# Revit family: HOSPITAIR PACK - 11 bar - 15 bar
name_source: partatom
category: Equipement de génie climatique
revit_build: Autodesk Revit 2018 (Build: 20170223_1515(x64)
units: mm (PartAtom-declared; Revit-internal decimal feet)

## family parameters
Basée sur le plan de construction = Non
Classification = Aucun
Cote de connecteur circulaire = Utiliser le diamètre
Couper avec des vides une fois chargée = Non
Partagée = Non
Point de calcul de pièce = Non
Toujours verticalement = Oui
Type d'élément = Normal

## types (30) — shared parameters
COS_PHI_COFFRET = 0.9
COS_PHI_COMPRESSEUR = 0.9
NBR_POLES_COFFRET_CONNEXION_X' = 1
NBR_POLES_COFFRET_CONNEXION_Y' = 1
NBR_POLES_COFFRET_X = 1
NBR_POLES_COFFRET_Y = 1
NBR_POLES_COMPRESSEUR = 3
PUISS_ELECT_COFFRET = 0 kW
PUISS_ELECT_COFFRET' = 0 kW
TENSION_ALIM_COMPRESSEUR = 400 V

## per-type parameters (varying)
- HOSPITAIR PACK - 11 bar - MVX4 - Principal: BRANCHEMENT_TERRE_COFFRET_CONNEXION_X'=Non; BRANCHEMENT_TERRE_COFFRET_CONNEXION_Y'=Non; BRANCHEMENT_TERRE_COFFRET_X=Oui; BRANCHEMENT_TERRE_COFFRET_Y=Oui; BRANCHEMENT_TERRE_COMPRESSEUR=Oui; COFFRET ELEC STANDARD PM2=Oui; COMPRESSEUR=HOSPITAIR G - MVX 4-5 - MVA 9 - MVB 12-16 - MVC 19-23 : MVX 4; CONNEXION X'_Y'=Non; Chaine de traitement ...AD5035=Oui; Chaine de traitement ...AD5065=Non; Chaine de traitement ...AD5130=Non; Chaine de traitement ...AD5195=Non; DESCR_ALIM_COFFRET_CONNEXION_X'=NE PAS UTILISER; DESCR_ALIM_COFFRET_CONNEXION_Y'=NE PAS UTILISER; DESCR_ALIM_COFFRET_X=Alimentation électrique, 3G0.75mm²; DESCR_ALIM_COFFRET_Y=Alimentation électrique, 3G0.75mm²; DESCR_ALIM_COMPRESSEUR=Alimentation électrique, 4G2.5mm²; DESCR_REFOUL=Refoulement Air; 29m3/h; G1/2"FEM; DIAM_REFOUL_AIR=15 mm  [stored 0.0492126 ft]; Debit_refoulement_air=29.0 m³/h; HAUTEUR=1340 mm; HAUTEUR_COFFRET=1080 mm  [stored 3.54331 ft]; HAUTEUR_SORTIE_AIR=1372 mm; LARGEUR=600 mm  [stored 1.9685 ft]; LARGEUR_COFFRET_GAUCHE=300 mm  [stored 0.984252 ft]; LARGEUR_SORTIE_AIR=25 mm  [stored 0.082021 ft]; LONGUEUR=860 mm; LONGUEUR_COFFRET_GAUCHE=344 mm; MAINTENANCE_ZONE_ARRIERE=1135 mm; MAINTENANCE_ZONE_AVANT=720 mm; MAINTENANCE_ZONE_GAUCHE-DROITE=2190 mm; MAINTENANCE_ZONE_HAUTEUR=1780 mm; NEUTRE_COFFRET_CONNEXION_X'=Non; NEUTRE_COFFRET_CONNEXION_Y'=Non; NEUTRE_COFFRET_X=Oui; NEUTRE_COFFRET_Y=Oui; NIVEAU_SONORE(dB(A))=62; POIDS(Kg)=170 mm  [stored 0.557743 ft]; PUISS_APPARENTE_COFFRET=333 VA; PUISS_APPARENTE_COFFRET'=0 VA; PUISS_APPARENTE_COMPRESSEUR=4444 VA; PUISS_ELECT_COMPRESSEUR=4 kW; TENSION_ALIM_COFFRET=230 V; Zone de maintenance=Oui
- HOSPITAIR PACK - 11 bar - MVX5 - Principal: BRANCHEMENT_TERRE_COFFRET_CONNEXION_X'=Non; BRANCHEMENT_TERRE_COFFRET_CONNEXION_Y'=Non; BRANCHEMENT_TERRE_COFFRET_X=Oui; BRANCHEMENT_TERRE_COFFRET_Y=Oui; BRANCHEMENT_TERRE_COMPRESSEUR=Oui; COFFRET ELEC STANDARD PM2=Oui; COMPRESSEUR=HOSPITAIR G - MVX 4-5 - MVA 9 - MVB 12-16 - MVC 19-23 : MVX 5; CONNEXION X'_Y'=Non; Chaine de traitement ...AD5035=Non; Chaine de traitement ...AD5065=Oui; Chaine de traitement ...AD5130=Non; Chaine de traitement ...AD5195=Non; DESCR_ALIM_COFFRET_CONNEXION_X'=NE PAS UTILISER; DESCR_ALIM_COFFRET_CONNEXION_Y'=NE PAS UTILISER; DESCR_ALIM_COFFRET_X=Alimentation électrique, 3G0.75mm²; DESCR_ALIM_COFFRET_Y=Alimentation électrique, 3G0.75mm²; DESCR_ALIM_COMPRESSEUR=Alimentation électrique, 4G2.5mm²; DESCR_REFOUL=Refoulement Air; 40m3/h; G1/2"FEM; DIAM_REFOUL_AIR=15 mm  [stored 0.0492126 ft]; Debit_refoulement_air=40.0 m³/h; HAUTEUR=1430 mm; HAUTEUR_COFFRET=1365 mm; HAUTEUR_SORTIE_AIR=1662 mm; LARGEUR=600 mm  [stored 1.9685 ft]; LARGEUR_COFFRET_GAUCHE=300 mm  [stored 0.984252 ft]; LARGEUR_SORTIE_AIR=20 mm  [stored 0.0656168 ft]; LONGUEUR=870 mm  [stored 2.85433 ft]; LONGUEUR_COFFRET_GAUCHE=344 mm; MAINTENANCE_ZONE_ARRIERE=1135 mm; MAINTENANCE_ZONE_AVANT=720 mm; MAINTENANCE_ZONE_GAUCHE-DROITE=2190 mm; MAINTENANCE_ZONE_HAUTEUR=2065 mm; NEUTRE_COFFRET_CONNEXION_X'=Non; NEUTRE_COFFRET_CONNEXION_Y'=Non; NEUTRE_COFFRET_X=Oui; NEUTRE_COFFRET_Y=Oui; NIVEAU_SONORE(dB(A))=64; POIDS(Kg)=185 mm  [stored 0.606955 ft]; PUISS_APPARENTE_COFFRET=333 VA; PUISS_APPARENTE_COFFRET'=0 VA; PUISS_APPARENTE_COMPRESSEUR=6111 VA; PUISS_ELECT_COMPRESSEUR=6 kW; TENSION_ALIM_COFFRET=230 V; Zone de maintenance=Oui
- HOSPITAIR PACK - 11 bar - MVA9 - Principal: BRANCHEMENT_TERRE_COFFRET_CONNEXION_X'=Non; BRANCHEMENT_TERRE_COFFRET_CONNEXION_Y'=Non; BRANCHEMENT_TERRE_COFFRET_X=Oui; BRANCHEMENT_TERRE_COFFRET_Y=Oui; BRANCHEMENT_TERRE_COMPRESSEUR=Oui; COFFRET ELEC STANDARD PM2=Oui; COMPRESSEUR=HOSPITAIR G - MVX 4-5 - MVA 9 - MVB 12-16 - MVC 19-23 : MVA 9; CONNEXION X'_Y'=Non; Chaine de traitement ...AD5035=Non; Chaine de traitement ...AD5065=Oui; Chaine de traitement ...AD5130=Non; Chaine de traitement ...AD5195=Non; DESCR_ALIM_COFFRET_CONNEXION_X'=NE PAS UTILISER; DESCR_ALIM_COFFRET_CONNEXION_Y'=NE PAS UTILISER; DESCR_ALIM_COFFRET_X=Alimentation électrique, 3G0.75mm²; DESCR_ALIM_COFFRET_Y=Alimentation électrique, 3G0.75mm²; DESCR_ALIM_COMPRESSEUR=Alimentation électrique, 4G4mm²; DESCR_REFOUL=Refoulement Air; 65m3/h; G1/2"FEM; DIAM_REFOUL_AIR=15 mm  [stored 0.0492126 ft]; Debit_refoulement_air=65.0 m³/h; HAUTEUR=1630 mm; HAUTEUR_COFFRET=1365 mm; HAUTEUR_SORTIE_AIR=1662 mm; LARGEUR=640 mm  [stored 2.09974 ft]; LARGEUR_COFFRET_GAUCHE=300 mm  [stored 0.984252 ft]; LARGEUR_SORTIE_AIR=20 mm  [stored 0.0656168 ft]; LONGUEUR=1000 mm  [stored 3.28084 ft]; LONGUEUR_COFFRET_GAUCHE=344 mm; MAINTENANCE_ZONE_ARRIERE=1293 mm; MAINTENANCE_ZONE_AVANT=720 mm; MAINTENANCE_ZONE_GAUCHE-DROITE=2230 mm; MAINTENANCE_ZONE_HAUTEUR=2065 mm; NEUTRE_COFFRET_CONNEXION_X'=Non; NEUTRE_COFFRET_CONNEXION_Y'=Non; NEUTRE_COFFRET_X=Oui; NEUTRE_COFFRET_Y=Oui; NIVEAU_SONORE(dB(A))=65; POIDS(Kg)=290 mm  [stored 0.951444 ft]; PUISS_APPARENTE_COFFRET=333 VA; PUISS_APPARENTE_COFFRET'=0 VA; PUISS_APPARENTE_COMPRESSEUR=8333 VA; PUISS_ELECT_COMPRESSEUR=8 kW; TENSION_ALIM_COFFRET=230 V; Zone de maintenance=Oui
- HOSPITAIR PACK - 11 bar - MVX3 -  Principal: BRANCHEMENT_TERRE_COFFRET_CONNEXION_X'=Non; BRANCHEMENT_TERRE_COFFRET_CONNEXION_Y'=Non; BRANCHEMENT_TERRE_COFFRET_X=Oui; BRANCHEMENT_TERRE_COFFRET_Y=Oui; BRANCHEMENT_TERRE_COMPRESSEUR=Oui; COFFRET ELEC STANDARD PM2=Oui; COMPRESSEUR=HOSPITAIR G - MVX 4-5 - MVA 9 - MVB 12-16 - MVC 19-23 : MVX 4; CONNEXION X'_Y'=Non; Chaine de traitement ...AD5035=Oui; Chaine de traitement ...AD5065=Non; Chaine de traitement ...AD5130=Non; Chaine de traitement ...AD5195=Non; DESCR_ALIM_COFFRET_CONNEXION_X'=NE PAS UTILISER; DESCR_ALIM_COFFRET_CONNEXION_Y'=NE PAS UTILISER; DESCR_ALIM_COFFRET_X=Alimentation électrique, 3G0.75mm²; DESCR_ALIM_COFFRET_Y=Alimentation électrique, 3G0.75mm²; DESCR_ALIM_COMPRESSEUR=Alimentation électrique, 4G2.5mm²; DESCR_REFOUL=Refoulement Air; 22m3/h; G1/2"FEM; DIAM_REFOUL_AIR=15 mm  [stored 0.0492126 ft]; Debit_refoulement_air=22.0 m³/h; HAUTEUR=1340 mm; HAUTEUR_COFFRET=1080 mm  [stored 3.54331 ft]; HAUTEUR_SORTIE_AIR=1372 mm; LARGEUR=600 mm  [stored 1.9685 ft]; LARGEUR_COFFRET_GAUCHE=300 mm  [stored 0.984252 ft]; LARGEUR_SORTIE_AIR=25 mm  [stored 0.082021 ft]; LONGUEUR=860 mm; LONGUEUR_COFFRET_GAUCHE=344 mm; MAINTENANCE_ZONE_ARRIERE=1135 mm; MAINTENANCE_ZONE_AVANT=720 mm; MAINTENANCE_ZONE_GAUCHE-DROITE=2190 mm; MAINTENANCE_ZONE_HAUTEUR=1780 mm; NEUTRE_COFFRET_CONNEXION_X'=Non; NEUTRE_COFFRET_CONNEXION_Y'=Non; NEUTRE_COFFRET_X=Oui; NEUTRE_COFFRET_Y=Oui; NIVEAU_SONORE(dB(A))=61; POIDS(Kg)=165 mm; PUISS_APPARENTE_COFFRET=333 VA; PUISS_APPARENTE_COFFRET'=0 VA; PUISS_APPARENTE_COMPRESSEUR=3333 VA; PUISS_ELECT_COMPRESSEUR=3 kW; TENSION_ALIM_COFFRET=230 V; Zone de maintenance=Oui
- HOSPITAIR PACK - 11 bar - MVX2 - Principal: BRANCHEMENT_TERRE_COFFRET_CONNEXION_X'=Non; BRANCHEMENT_TERRE_COFFRET_CONNEXION_Y'=Non; BRANCHEMENT_TERRE_COFFRET_X=Oui; BRANCHEMENT_TERRE_COFFRET_Y=Oui; BRANCHEMENT_TERRE_COMPRESSEUR=Oui; COFFRET ELEC STANDARD PM2=Oui; COMPRESSEUR=HOSPITAIR G - MVX 4-5 - MVA 9 - MVB 12-16 - MVC 19-23 : MVX 4; CONNEXION X'_Y'=Non; Chaine de traitement ...AD5035=Oui; Chaine de traitement ...AD5065=Non; Chaine de traitement ...AD5130=Non; Chaine de traitement ...AD5195=Non; DESCR_ALIM_COFFRET_CONNEXION_X'=NE PAS UTILISER; DESCR_ALIM_COFFRET_CONNEXION_Y'=NE PAS UTILISER; DESCR_ALIM_COFFRET_X=Alimentation électrique, 3G0.75mm²; DESCR_ALIM_COFFRET_Y=Alimentation électrique, 3G0.75mm²; DESCR_ALIM_COMPRESSEUR=Alimentation électrique, 4G2.5mm²; DESCR_REFOUL=Refoulement Air; 16m3/h; G1/2"FEM; DIAM_REFOUL_AIR=15 mm  [stored 0.0492126 ft]; Debit_refoulement_air=16.0 m³/h; HAUTEUR=1340 mm; HAUTEUR_COFFRET=1080 mm  [stored 3.54331 ft]; HAUTEUR_SORTIE_AIR=1372 mm; LARGEUR=600 mm  [stored 1.9685 ft]; LARGEUR_COFFRET_GAUCHE=300 mm  [stored 0.984252 ft]; LARGEUR_SORTIE_AIR=25 mm  [stored 0.082021 ft]; LONGUEUR=860 mm; LONGUEUR_COFFRET_GAUCHE=344 mm; MAINTENANCE_ZONE_ARRIERE=1135 mm; MAINTENANCE_ZONE_AVANT=720 mm; MAINTENANCE_ZONE_GAUCHE-DROITE=2190 mm; MAINTENANCE_ZONE_HAUTEUR=1780 mm; NEUTRE_COFFRET_CONNEXION_X'=Non; NEUTRE_COFFRET_CONNEXION_Y'=Non; NEUTRE_COFFRET_X=Oui; NEUTRE_COFFRET_Y=Oui; NIVEAU_SONORE(dB(A))=60; POIDS(Kg)=165 mm; PUISS_APPARENTE_COFFRET=333 VA; PUISS_APPARENTE_COFFRET'=0 VA; PUISS_APPARENTE_COMPRESSEUR=2444 VA; PUISS_ELECT_COMPRESSEUR=2 kW; TENSION_ALIM_COFFRET=230 V; Zone de maintenance=Non
- HOSPITAIR PACK - 11 bar - MVB12 - Principal: BRANCHEMENT_TERRE_COFFRET_CONNEXION_X'=Non; BRANCHEMENT_TERRE_COFFRET_CONNEXION_Y'=Non; BRANCHEMENT_TERRE_COFFRET_X=Oui; BRANCHEMENT_TERRE_COFFRET_Y=Oui; BRANCHEMENT_TERRE_COMPRESSEUR=Oui; COFFRET ELEC STANDARD PM2=Oui; COMPRESSEUR=HOSPITAIR G - MVX 4-5 - MVA 9 - MVB 12-16 - MVC 19-23 : MVB 12; CONNEXION X'_Y'=Non; Chaine de traitement ...AD5035=Non; Chaine de traitement ...AD5065=Non; Chaine de traitement ...AD5130=Oui; Chaine de traitement ...AD5195=Non; DESCR_ALIM_COFFRET_CONNEXION_X'=NE PAS UTILISER; DESCR_ALIM_COFFRET_CONNEXION_Y'=NE PAS UTILISER; DESCR_ALIM_COFFRET_X=Alimentation électrique, 3G0.75mm²; DESCR_ALIM_COFFRET_Y=Alimentation électrique, 3G0.75mm²; DESCR_ALIM_COMPRESSEUR=Alimentation électrique, 4G6mm²; DESCR_REFOUL=Refoulement Air; 100m3/h; G3/4"FEM; DIAM_REFOUL_AIR=20 mm  [stored 0.0656168 ft]; Debit_refoulement_air=100.0 m³/h; HAUTEUR=1350 mm; HAUTEUR_COFFRET=1365 mm; HAUTEUR_SORTIE_AIR=1662 mm; LARGEUR=750 mm  [stored 2.46063 ft]; LARGEUR_COFFRET_GAUCHE=370 mm  [stored 1.21391 ft]; LARGEUR_SORTIE_AIR=95 mm  [stored 0.31168 ft]; LONGUEUR=1100 mm; LONGUEUR_COFFRET_GAUCHE=344 mm; MAINTENANCE_ZONE_ARRIERE=1398 mm; MAINTENANCE_ZONE_AVANT=792.5 mm; MAINTENANCE_ZONE_GAUCHE-DROITE=2350 mm; MAINTENANCE_ZONE_HAUTEUR=2065 mm; NEUTRE_COFFRET_CONNEXION_X'=Non; NEUTRE_COFFRET_CONNEXION_Y'=Non; NEUTRE_COFFRET_X=Oui; NEUTRE_COFFRET_Y=Oui; NIVEAU_SONORE(dB(A))=64; POIDS(Kg)=375 mm  [stored 1.23031 ft]; PUISS_APPARENTE_COFFRET=333 VA; PUISS_APPARENTE_COFFRET'=0 VA; PUISS_APPARENTE_COMPRESSEUR=12222 VA; PUISS_ELECT_COMPRESSEUR=11 kW; TENSION_ALIM_COFFRET=230 V; Zone de maintenance=Oui
- HOSPITAIR PACK - 11 bar - MVC19 - Principal: BRANCHEMENT_TERRE_COFFRET_CONNEXION_X'=Oui; BRANCHEMENT_TERRE_COFFRET_CONNEXION_Y'=Oui; BRANCHEMENT_TERRE_COFFRET_X=Non; BRANCHEMENT_TERRE_COFFRET_Y=Non; BRANCHEMENT_TERRE_COMPRESSEUR=Oui; COFFRET ELEC STANDARD PM2=Oui; COMPRESSEUR=HOSPITAIR G - MVX 4-5 - MVA 9 - MVB 12-16 - MVC 19-23 : MVC 19; CONNEXION X'_Y'=Oui; Chaine de traitement ...AD5035=Non; Chaine de traitement ...AD5065=Non; Chaine de traitement ...AD5130=Non; Chaine de traitement ...AD5195=Oui; DESCR_ALIM_COFFRET_CONNEXION_X'=Alimentation électrique, 3G0.75mm²; DESCR_ALIM_COFFRET_CONNEXION_Y'=Alimentation électrique, 3G0.75mm²; DESCR_ALIM_COFFRET_X=NE PAS UTILISER; DESCR_ALIM_COFFRET_Y=NE PAS UTILISER; DESCR_ALIM_COMPRESSEUR=Alimentation électrique, 4G10mm²; DESCR_REFOUL=Refoulement Air; 179m3/h; G3/4"FEM; DIAM_REFOUL_AIR=20 mm  [stored 0.0656168 ft]; Debit_refoulement_air=179.0 m³/h; HAUTEUR=1670 mm; HAUTEUR_COFFRET=1550 mm; HAUTEUR_SORTIE_AIR=1662 mm; LARGEUR=890 mm  [stored 2.91995 ft]; LARGEUR_COFFRET_GAUCHE=400 mm  [stored 1.31234 ft]; LARGEUR_SORTIE_AIR=10 mm  [stored 0.0328084 ft]; LONGUEUR=1870 mm; LONGUEUR_COFFRET_GAUCHE=1048 mm; MAINTENANCE_ZONE_ARRIERE=1593 mm; MAINTENANCE_ZONE_AVANT=792.5 mm; MAINTENANCE_ZONE_GAUCHE-DROITE=2400 mm; MAINTENANCE_ZONE_HAUTEUR=2250 mm; NEUTRE_COFFRET_CONNEXION_X'=Oui; NEUTRE_COFFRET_CONNEXION_Y'=Oui; NEUTRE_COFFRET_X=Non; NEUTRE_COFFRET_Y=Non; NIVEAU_SONORE(dB(A))=67; POIDS(Kg)=660 mm  [stored 2.16535 ft]; PUISS_APPARENTE_COFFRET=0 VA; PUISS_APPARENTE_COFFRET'=333 VA; PUISS_APPARENTE_COMPRESSEUR=20556 VA; PUISS_ELECT_COMPRESSEUR=19 kW; TENSION_ALIM_COFFRET=230 V; Zone de maintenance=Oui
- HOSPITAIR PACK - 11 bar - MVB16 - Principal: BRANCHEMENT_TERRE_COFFRET_CONNEXION_X'=Non; BRANCHEMENT_TERRE_COFFRET_CONNEXION_Y'=Non; BRANCHEMENT_TERRE_COFFRET_X=Oui; BRANCHEMENT_TERRE_COFFRET_Y=Oui; BRANCHEMENT_TERRE_COMPRESSEUR=Oui; COFFRET ELEC STANDARD PM2=Oui; COMPRESSEUR=HOSPITAIR G - MVX 4-5 - MVA 9 - MVB 12-16 - MVC 19-23 : MVB 16; CONNEXION X'_Y'=Non; Chaine de traitement ...AD5035=Non; Chaine de traitement ...AD5065=Non; Chaine de traitement ...AD5130=Oui; Chaine de traitement ...AD5195=Non; DESCR_ALIM_COFFRET_CONNEXION_X'=NE PAS UTILISER; DESCR_ALIM_COFFRET_CONNEXION_Y'=NE PAS UTILISER; DESCR_ALIM_COFFRET_X=Alimentation électrique, 3G0.75mm²; DESCR_ALIM_COFFRET_Y=Alimentation électrique, 3G0.75mm²; DESCR_ALIM_COMPRESSEUR=Alimentation électrique, 4G10mm²; DESCR_REFOUL=Refoulement Air; 126m3/h; G3/4"FEM; DIAM_REFOUL_AIR=20 mm  [stored 0.0656168 ft]; Debit_refoulement_air=126.0 m³/h; HAUTEUR=1350 mm; HAUTEUR_COFFRET=1365 mm; HAUTEUR_SORTIE_AIR=1662 mm; LARGEUR=750 mm  [stored 2.46063 ft]; LARGEUR_COFFRET_GAUCHE=370 mm  [stored 1.21391 ft]; LARGEUR_SORTIE_AIR=95 mm  [stored 0.31168 ft]; LONGUEUR=1250 mm  [stored 4.10105 ft]; LONGUEUR_COFFRET_GAUCHE=344 mm; MAINTENANCE_ZONE_ARRIERE=1398 mm; MAINTENANCE_ZONE_AVANT=792.5 mm; MAINTENANCE_ZONE_GAUCHE-DROITE=2350 mm; MAINTENANCE_ZONE_HAUTEUR=2065 mm; NEUTRE_COFFRET_CONNEXION_X'=Non; NEUTRE_COFFRET_CONNEXION_Y'=Non; NEUTRE_COFFRET_X=Oui; NEUTRE_COFFRET_Y=Oui; NIVEAU_SONORE(dB(A))=65; POIDS(Kg)=480 mm  [stored 1.5748 ft]; PUISS_APPARENTE_COFFRET=333 VA; PUISS_APPARENTE_COFFRET'=0 VA; PUISS_APPARENTE_COMPRESSEUR=16667 VA; PUISS_ELECT_COMPRESSEUR=15 kW; TENSION_ALIM_COFFRET=230 V; Zone de maintenance=Oui
- HOSPITAIR PACK - 15 bar - MVC23 - Principal: BRANCHEMENT_TERRE_COFFRET_CONNEXION_X'=Oui; BRANCHEMENT_TERRE_COFFRET_CONNEXION_Y'=Oui; BRANCHEMENT_TERRE_COFFRET_X=Non; BRANCHEMENT_TERRE_COFFRET_Y=Non; BRANCHEMENT_TERRE_COMPRESSEUR=Oui; COFFRET ELEC STANDARD PM2=Oui; COMPRESSEUR=HOSPITAIR G - MVX 4-5 - MVA 9 - MVB 12-16 - MVC 19-23 : MVC 23; CONNEXION X'_Y'=Oui; Chaine de traitement ...AD5035=Non; Chaine de traitement ...AD5065=Non; Chaine de traitement ...AD5130=Non; Chaine de traitement ...AD5195=Oui; DESCR_ALIM_COFFRET_CONNEXION_X'=Alimentation électrique, 3G0.75mm²; DESCR_ALIM_COFFRET_CONNEXION_Y'=Alimentation électrique, 3G0.75mm²; DESCR_ALIM_COFFRET_X=NE PAS UTILISER; DESCR_ALIM_COFFRET_Y=NE PAS UTILISER; DESCR_ALIM_COMPRESSEUR=Alimentation électrique, 4G16mm²; DESCR_REFOUL=Refoulement Air; 174m3/h; G3/4"FEM; DIAM_REFOUL_AIR=20 mm  [stored 0.0656168 ft]; Debit_refoulement_air=174.0 m³/h; HAUTEUR=1670 mm; HAUTEUR_COFFRET=1550 mm; HAUTEUR_SORTIE_AIR=1662 mm; LARGEUR=890 mm  [stored 2.91995 ft]; LARGEUR_COFFRET_GAUCHE=400 mm  [stored 1.31234 ft]; LARGEUR_SORTIE_AIR=10 mm  [stored 0.0328084 ft]; LONGUEUR=1870 mm; LONGUEUR_COFFRET_GAUCHE=1048 mm; MAINTENANCE_ZONE_ARRIERE=1593 mm; MAINTENANCE_ZONE_AVANT=792.5 mm; MAINTENANCE_ZONE_GAUCHE-DROITE=2400 mm; MAINTENANCE_ZONE_HAUTEUR=2250 mm; NEUTRE_COFFRET_CONNEXION_X'=Oui; NEUTRE_COFFRET_CONNEXION_Y'=Oui; NEUTRE_COFFRET_X=Non; NEUTRE_COFFRET_Y=Non; NIVEAU_SONORE(dB(A))=69; POIDS(Kg)=690 mm  [stored 2.26378 ft]; PUISS_APPARENTE_COFFRET=0 VA; PUISS_APPARENTE_COFFRET'=333 VA; PUISS_APPARENTE_COMPRESSEUR=24444 VA; PUISS_ELECT_COMPRESSEUR=22 kW; TENSION_ALIM_COFFRET=230 V; Zone de maintenance=Oui
- HOSPITAIR PACK - 11 bar - MVX2 - Secondaire: BRANCHEMENT_TERRE_COFFRET_CONNEXION_X'=Non; BRANCHEMENT_TERRE_COFFRET_CONNEXION_Y'=Non; BRANCHEMENT_TERRE_COFFRET_X=Non; BRANCHEMENT_TERRE_COFFRET_Y=Non; BRANCHEMENT_TERRE_COMPRESSEUR=Non; COFFRET ELEC STANDARD PM2=Non; COMPRESSEUR=HOSPITAIR G - MVX 4-5 - MVA 9 - MVB 12-16 - MVC 19-23 : MVX 4; CONNEXION X'_Y'=Non; Chaine de traitement ...AD5035=Oui; Chaine de traitement ...AD5065=Non; Chaine de traitement ...AD5130=Non; Chaine de traitement ...AD5195=Non; DESCR_ALIM_COFFRET_CONNEXION_X'=NE PAS UTILISER; DESCR_ALIM_COFFRET_CONNEXION_Y'=NE PAS UTILISER; DESCR_ALIM_COFFRET_X=NE PAS UTILISER; DESCR_ALIM_COFFRET_Y=NE PAS UTILISER; DESCR_ALIM_COMPRESSEUR=Alimentation électrique, 4G2.5mm²; DESCR_REFOUL=Refoulement Air; 16m3/h; G1/2"FEM; DIAM_REFOUL_AIR=15 mm  [stored 0.0492126 ft]; Debit_refoulement_air=16.0 m³/h; HAUTEUR=1340 mm; HAUTEUR_COFFRET=1080 mm  [stored 3.54331 ft]; HAUTEUR_SORTIE_AIR=1372 mm; LARGEUR=600 mm  [stored 1.9685 ft]; LARGEUR_COFFRET_GAUCHE=300 mm  [stored 0.984252 ft]; LARGEUR_SORTIE_AIR=25 mm  [stored 0.082021 ft]; LONGUEUR=860 mm; LONGUEUR_COFFRET_GAUCHE=344 mm; MAINTENANCE_ZONE_ARRIERE=1135 mm; MAINTENANCE_ZONE_AVANT=720 mm; MAINTENANCE_ZONE_GAUCHE-DROITE=2190 mm; MAINTENANCE_ZONE_HAUTEUR=1780 mm; NEUTRE_COFFRET_CONNEXION_X'=Non; NEUTRE_COFFRET_CONNEXION_Y'=Non; NEUTRE_COFFRET_X=Non; NEUTRE_COFFRET_Y=Non; NIVEAU_SONORE(dB(A))=60; POIDS(Kg)=155 mm  [stored 0.50853 ft]; PUISS_APPARENTE_COFFRET=0 VA; PUISS_APPARENTE_COFFRET'=0 VA; PUISS_APPARENTE_COMPRESSEUR=2444 VA; PUISS_ELECT_COMPRESSEUR=2 kW; TENSION_ALIM_COFFRET=0 V; Zone de maintenance=Oui
- HOSPITAIR PACK - 11 bar - MVX3 - Secondaire: BRANCHEMENT_TERRE_COFFRET_CONNEXION_X'=Non; BRANCHEMENT_TERRE_COFFRET_CONNEXION_Y'=Non; BRANCHEMENT_TERRE_COFFRET_X=Non; BRANCHEMENT_TERRE_COFFRET_Y=Non; BRANCHEMENT_TERRE_COMPRESSEUR=Oui; COFFRET ELEC STANDARD PM2=Non; COMPRESSEUR=HOSPITAIR G - MVX 4-5 - MVA 9 - MVB 12-16 - MVC 19-23 : MVX 4; CONNEXION X'_Y'=Non; Chaine de traitement ...AD5035=Oui; Chaine de traitement ...AD5065=Non; Chaine de traitement ...AD5130=Non; Chaine de traitement ...AD5195=Non; DESCR_ALIM_COFFRET_CONNEXION_X'=NE PAS UTILISER; DESCR_ALIM_COFFRET_CONNEXION_Y'=NE PAS UTILISER; DESCR_ALIM_COFFRET_X=NE PAS UTILISER; DESCR_ALIM_COFFRET_Y=NE PAS UTILISER; DESCR_ALIM_COMPRESSEUR=Alimentation électrique, 4G2.5mm²; DESCR_REFOUL=Refoulement Air; 22m3/h; G1/2"FEM; DIAM_REFOUL_AIR=15 mm  [stored 0.0492126 ft]; Debit_refoulement_air=22.0 m³/h; HAUTEUR=1340 mm; HAUTEUR_COFFRET=1080 mm  [stored 3.54331 ft]; HAUTEUR_SORTIE_AIR=1372 mm; LARGEUR=600 mm  [stored 1.9685 ft]; LARGEUR_COFFRET_GAUCHE=300 mm  [stored 0.984252 ft]; LARGEUR_SORTIE_AIR=25 mm  [stored 0.082021 ft]; LONGUEUR=860 mm; LONGUEUR_COFFRET_GAUCHE=344 mm; MAINTENANCE_ZONE_ARRIERE=1135 mm; MAINTENANCE_ZONE_AVANT=720 mm; MAINTENANCE_ZONE_GAUCHE-DROITE=2190 mm; MAINTENANCE_ZONE_HAUTEUR=1780 mm; NEUTRE_COFFRET_CONNEXION_X'=Non; NEUTRE_COFFRET_CONNEXION_Y'=Non; NEUTRE_COFFRET_X=Non; NEUTRE_COFFRET_Y=Non; NIVEAU_SONORE(dB(A))=61; POIDS(Kg)=155 mm  [stored 0.50853 ft]; PUISS_APPARENTE_COFFRET=0 VA; PUISS_APPARENTE_COFFRET'=0 VA; PUISS_APPARENTE_COMPRESSEUR=3333 VA; PUISS_ELECT_COMPRESSEUR=3 kW; TENSION_ALIM_COFFRET=0 V; Zone de maintenance=Oui
- HOSPITAIR PACK - 11 bar - MVX4 - Secondaire: BRANCHEMENT_TERRE_COFFRET_CONNEXION_X'=Non; BRANCHEMENT_TERRE_COFFRET_CONNEXION_Y'=Non; BRANCHEMENT_TERRE_COFFRET_X=Non; BRANCHEMENT_TERRE_COFFRET_Y=Non; BRANCHEMENT_TERRE_COMPRESSEUR=Oui; COFFRET ELEC STANDARD PM2=Non; COMPRESSEUR=HOSPITAIR G - MVX 4-5 - MVA 9 - MVB 12-16 - MVC 19-23 : MVX 4; CONNEXION X'_Y'=Non; Chaine de traitement ...AD5035=Oui; Chaine de traitement ...AD5065=Non; Chaine de traitement ...AD5130=Non; Chaine de traitement ...AD5195=Non; DESCR_ALIM_COFFRET_CONNEXION_X'=NE PAS UTILISER; DESCR_ALIM_COFFRET_CONNEXION_Y'=NE PAS UTILISER; DESCR_ALIM_COFFRET_X=NE PAS UTILISER; DESCR_ALIM_COFFRET_Y=NE PAS UTILISER; DESCR_ALIM_COMPRESSEUR=Alimentation électrique, 4G2.5mm²; DESCR_REFOUL=Refoulement Air; 29m3/h; G1/2"FEM; DIAM_REFOUL_AIR=15 mm  [stored 0.0492126 ft]; Debit_refoulement_air=29.0 m³/h; HAUTEUR=1340 mm; HAUTEUR_COFFRET=1080 mm  [stored 3.54331 ft]; HAUTEUR_SORTIE_AIR=1372 mm; LARGEUR=600 mm  [stored 1.9685 ft]; LARGEUR_COFFRET_GAUCHE=300 mm  [stored 0.984252 ft]; LARGEUR_SORTIE_AIR=25 mm  [stored 0.082021 ft]; LONGUEUR=860 mm; LONGUEUR_COFFRET_GAUCHE=344 mm; MAINTENANCE_ZONE_ARRIERE=1135 mm; MAINTENANCE_ZONE_AVANT=720 mm; MAINTENANCE_ZONE_GAUCHE-DROITE=2190 mm; MAINTENANCE_ZONE_HAUTEUR=1780 mm; NEUTRE_COFFRET_CONNEXION_X'=Non; NEUTRE_COFFRET_CONNEXION_Y'=Non; NEUTRE_COFFRET_X=Non; NEUTRE_COFFRET_Y=Non; NIVEAU_SONORE(dB(A))=62; POIDS(Kg)=160 mm  [stored 0.524934 ft]; PUISS_APPARENTE_COFFRET=0 VA; PUISS_APPARENTE_COFFRET'=0 VA; PUISS_APPARENTE_COMPRESSEUR=4444 VA; PUISS_ELECT_COMPRESSEUR=4 kW; TENSION_ALIM_COFFRET=0 V; Zone de maintenance=Oui
- HOSPITAIR PACK - 11 bar - MVX5 - Secondaire: BRANCHEMENT_TERRE_COFFRET_CONNEXION_X'=Non; BRANCHEMENT_TERRE_COFFRET_CONNEXION_Y'=Non; BRANCHEMENT_TERRE_COFFRET_X=Non; BRANCHEMENT_TERRE_COFFRET_Y=Non; BRANCHEMENT_TERRE_COMPRESSEUR=Oui; COFFRET ELEC STANDARD PM2=Non; COMPRESSEUR=HOSPITAIR G - MVX 4-5 - MVA 9 - MVB 12-16 - MVC 19-23 : MVX 5; CONNEXION X'_Y'=Non; Chaine de traitement ...AD5035=Non; Chaine de traitement ...AD5065=Oui; Chaine de traitement ...AD5130=Non; Chaine de traitement ...AD5195=Non; DESCR_ALIM_COFFRET_CONNEXION_X'=NE PAS UTILISER; DESCR_ALIM_COFFRET_CONNEXION_Y'=NE PAS UTILISER; DESCR_ALIM_COFFRET_X=NE PAS UTILISER; DESCR_ALIM_COFFRET_Y=NE PAS UTILISER; DESCR_ALIM_COMPRESSEUR=Alimentation électrique, 4G2.5mm²; DESCR_REFOUL=Refoulement Air; 40m3/h; G1/2"FEM; DIAM_REFOUL_AIR=15 mm  [stored 0.0492126 ft]; Debit_refoulement_air=40.0 m³/h; HAUTEUR=1430 mm; HAUTEUR_COFFRET=1365 mm; HAUTEUR_SORTIE_AIR=1662 mm; LARGEUR=600 mm  [stored 1.9685 ft]; LARGEUR_COFFRET_GAUCHE=300 mm  [stored 0.984252 ft]; LARGEUR_SORTIE_AIR=20 mm  [stored 0.0656168 ft]; LONGUEUR=870 mm  [stored 2.85433 ft]; LONGUEUR_COFFRET_GAUCHE=344 mm; MAINTENANCE_ZONE_ARRIERE=1135 mm; MAINTENANCE_ZONE_AVANT=720 mm; MAINTENANCE_ZONE_GAUCHE-DROITE=2190 mm; MAINTENANCE_ZONE_HAUTEUR=2065 mm; NEUTRE_COFFRET_CONNEXION_X'=Non; NEUTRE_COFFRET_CONNEXION_Y'=Non; NEUTRE_COFFRET_X=Non; NEUTRE_COFFRET_Y=Non; NIVEAU_SONORE(dB(A))=64; POIDS(Kg)=175 mm  [stored 0.574147 ft]; PUISS_APPARENTE_COFFRET=0 VA; PUISS_APPARENTE_COFFRET'=0 VA; PUISS_APPARENTE_COMPRESSEUR=6111 VA; PUISS_ELECT_COMPRESSEUR=6 kW; TENSION_ALIM_COFFRET=0 V; Zone de maintenance=Oui
- HOSPITAIR PACK - 11 bar - MVA9 - Secondaire: BRANCHEMENT_TERRE_COFFRET_CONNEXION_X'=Non; BRANCHEMENT_TERRE_COFFRET_CONNEXION_Y'=Non; BRANCHEMENT_TERRE_COFFRET_X=Non; BRANCHEMENT_TERRE_COFFRET_Y=Non; BRANCHEMENT_TERRE_COMPRESSEUR=Oui; COFFRET ELEC STANDARD PM2=Non; COMPRESSEUR=HOSPITAIR G - MVX 4-5 - MVA 9 - MVB 12-16 - MVC 19-23 : MVA 9; CONNEXION X'_Y'=Non; Chaine de traitement ...AD5035=Non; Chaine de traitement ...AD5065=Oui; Chaine de traitement ...AD5130=Non; Chaine de traitement ...AD5195=Non; DESCR_ALIM_COFFRET_CONNEXION_X'=NE PAS UTILISER; DESCR_ALIM_COFFRET_CONNEXION_Y'=NE PAS UTILISER; DESCR_ALIM_COFFRET_X=NE PAS UTILISER; DESCR_ALIM_COFFRET_Y=NE PAS UTILISER; DESCR_ALIM_COMPRESSEUR=Alimentation électrique, 4G4mm²; DESCR_REFOUL=Refoulement Air; 65m3/h; G1/2"FEM; DIAM_REFOUL_AIR=15 mm  [stored 0.0492126 ft]; Debit_refoulement_air=65.0 m³/h; HAUTEUR=1630 mm; HAUTEUR_COFFRET=1365 mm; HAUTEUR_SORTIE_AIR=1662 mm; LARGEUR=640 mm  [stored 2.09974 ft]; LARGEUR_COFFRET_GAUCHE=300 mm  [stored 0.984252 ft]; LARGEUR_SORTIE_AIR=20 mm  [stored 0.0656168 ft]; LONGUEUR=1000 mm  [stored 3.28084 ft]; LONGUEUR_COFFRET_GAUCHE=344 mm; MAINTENANCE_ZONE_ARRIERE=1293 mm; MAINTENANCE_ZONE_AVANT=720 mm; MAINTENANCE_ZONE_GAUCHE-DROITE=2230 mm; MAINTENANCE_ZONE_HAUTEUR=2065 mm; NEUTRE_COFFRET_CONNEXION_X'=Non; NEUTRE_COFFRET_CONNEXION_Y'=Non; NEUTRE_COFFRET_X=Non; NEUTRE_COFFRET_Y=Non; NIVEAU_SONORE(dB(A))=65; POIDS(Kg)=280 mm  [stored 0.918635 ft]; PUISS_APPARENTE_COFFRET=0 VA; PUISS_APPARENTE_COFFRET'=0 VA; PUISS_APPARENTE_COMPRESSEUR=8333 VA; PUISS_ELECT_COMPRESSEUR=8 kW; TENSION_ALIM_COFFRET=0 V; Zone de maintenance=Oui
- HOSPITAIR PACK - 11 bar - MVB12 - Secondaire: BRANCHEMENT_TERRE_COFFRET_CONNEXION_X'=Non; BRANCHEMENT_TERRE_COFFRET_CONNEXION_Y'=Non; BRANCHEMENT_TERRE_COFFRET_X=Non; BRANCHEMENT_TERRE_COFFRET_Y=Non; BRANCHEMENT_TERRE_COMPRESSEUR=Oui; COFFRET ELEC STANDARD PM2=Non; COMPRESSEUR=HOSPITAIR G - MVX 4-5 - MVA 9 - MVB 12-16 - MVC 19-23 : MVB 12; CONNEXION X'_Y'=Non; Chaine de traitement ...AD5035=Non; Chaine de traitement ...AD5065=Non; Chaine de traitement ...AD5130=Oui; Chaine de traitement ...AD5195=Non; DESCR_ALIM_COFFRET_CONNEXION_X'=NE PAS UTILISER; DESCR_ALIM_COFFRET_CONNEXION_Y'=NE PAS UTILISER; DESCR_ALIM_COFFRET_X=NE PAS UTILISER; DESCR_ALIM_COFFRET_Y=NE PAS UTILISER; DESCR_ALIM_COMPRESSEUR=Alimentation électrique, 4G6mm²; DESCR_REFOUL=Refoulement Air; 100m3/h; G3/4"FEM; DIAM_REFOUL_AIR=20 mm  [stored 0.0656168 ft]; Debit_refoulement_air=100.0 m³/h; HAUTEUR=1350 mm; HAUTEUR_COFFRET=1365 mm; HAUTEUR_SORTIE_AIR=1662 mm; LARGEUR=750 mm  [stored 2.46063 ft]; LARGEUR_COFFRET_GAUCHE=370 mm  [stored 1.21391 ft]; LARGEUR_SORTIE_AIR=95 mm  [stored 0.31168 ft]; LONGUEUR=1100 mm; LONGUEUR_COFFRET_GAUCHE=344 mm; MAINTENANCE_ZONE_ARRIERE=1398 mm; MAINTENANCE_ZONE_AVANT=792.5 mm; MAINTENANCE_ZONE_GAUCHE-DROITE=2350 mm; MAINTENANCE_ZONE_HAUTEUR=2065 mm; NEUTRE_COFFRET_CONNEXION_X'=Non; NEUTRE_COFFRET_CONNEXION_Y'=Non; NEUTRE_COFFRET_X=Non; NEUTRE_COFFRET_Y=Non; NIVEAU_SONORE(dB(A))=64; POIDS(Kg)=365 mm  [stored 1.19751 ft]; PUISS_APPARENTE_COFFRET=0 VA; PUISS_APPARENTE_COFFRET'=0 VA; PUISS_APPARENTE_COMPRESSEUR=12222 VA; PUISS_ELECT_COMPRESSEUR=11 kW; TENSION_ALIM_COFFRET=0 V; Zone de maintenance=Oui
- HOSPITAIR PACK - 11 bar - MVB16 - Secondaire: BRANCHEMENT_TERRE_COFFRET_CONNEXION_X'=Non; BRANCHEMENT_TERRE_COFFRET_CONNEXION_Y'=Non; BRANCHEMENT_TERRE_COFFRET_X=Non; BRANCHEMENT_TERRE_COFFRET_Y=Non; BRANCHEMENT_TERRE_COMPRESSEUR=Oui; COFFRET ELEC STANDARD PM2=Non; COMPRESSEUR=HOSPITAIR G - MVX 4-5 - MVA 9 - MVB 12-16 - MVC 19-23 : MVB 16; CONNEXION X'_Y'=Non; Chaine de traitement ...AD5035=Non; Chaine de traitement ...AD5065=Non; Chaine de traitement ...AD5130=Oui; Chaine de traitement ...AD5195=Non; DESCR_ALIM_COFFRET_CONNEXION_X'=NE PAS UTILISER; DESCR_ALIM_COFFRET_CONNEXION_Y'=NE PAS UTILISER; DESCR_ALIM_COFFRET_X=NE PAS UTILISER; DESCR_ALIM_COFFRET_Y=NE PAS UTILISER; DESCR_ALIM_COMPRESSEUR=Alimentation électrique, 4G10mm²; DESCR_REFOUL=Refoulement Air; 126m3/h; G3/4"FEM; DIAM_REFOUL_AIR=20 mm  [stored 0.0656168 ft]; Debit_refoulement_air=126.0 m³/h; HAUTEUR=1350 mm; HAUTEUR_COFFRET=1365 mm; HAUTEUR_SORTIE_AIR=1662 mm; LARGEUR=750 mm  [stored 2.46063 ft]; LARGEUR_COFFRET_GAUCHE=370 mm  [stored 1.21391 ft]; LARGEUR_SORTIE_AIR=95 mm  [stored 0.31168 ft]; LONGUEUR=1250 mm  [stored 4.10105 ft]; LONGUEUR_COFFRET_GAUCHE=344 mm; MAINTENANCE_ZONE_ARRIERE=1398 mm; MAINTENANCE_ZONE_AVANT=792.5 mm; MAINTENANCE_ZONE_GAUCHE-DROITE=2350 mm; MAINTENANCE_ZONE_HAUTEUR=2065 mm; NEUTRE_COFFRET_CONNEXION_X'=Non; NEUTRE_COFFRET_CONNEXION_Y'=Non; NEUTRE_COFFRET_X=Non; NEUTRE_COFFRET_Y=Non; NIVEAU_SONORE(dB(A))=65; POIDS(Kg)=470 mm  [stored 1.54199 ft]; PUISS_APPARENTE_COFFRET=0 VA; PUISS_APPARENTE_COFFRET'=0 VA; PUISS_APPARENTE_COMPRESSEUR=16667 VA; PUISS_ELECT_COMPRESSEUR=15 kW; TENSION_ALIM_COFFRET=0 V; Zone de maintenance=Oui
- HOSPITAIR PACK - 11 bar - MVC19 - Secondaire: BRANCHEMENT_TERRE_COFFRET_CONNEXION_X'=Non; BRANCHEMENT_TERRE_COFFRET_CONNEXION_Y'=Non; BRANCHEMENT_TERRE_COFFRET_X=Non; BRANCHEMENT_TERRE_COFFRET_Y=Non; BRANCHEMENT_TERRE_COMPRESSEUR=Oui; COFFRET ELEC STANDARD PM2=Non; COMPRESSEUR=HOSPITAIR G - MVX 4-5 - MVA 9 - MVB 12-16 - MVC 19-23 : MVC 19; CONNEXION X'_Y'=Non; Chaine de traitement ...AD5035=Non; Chaine de traitement ...AD5065=Non; Chaine de traitement ...AD5130=Non; Chaine de traitement ...AD5195=Oui; DESCR_ALIM_COFFRET_CONNEXION_X'=NE PAS UTILISER; DESCR_ALIM_COFFRET_CONNEXION_Y'=NE PAS UTILISER; DESCR_ALIM_COFFRET_X=NE PAS UTILISER; DESCR_ALIM_COFFRET_Y=NE PAS UTILISER; DESCR_ALIM_COMPRESSEUR=Alimentation électrique, 4G10mm²; DESCR_REFOUL=Refoulement Air; 179m3/h; G3/4"FEM; DIAM_REFOUL_AIR=20 mm  [stored 0.0656168 ft]; Debit_refoulement_air=179.0 m³/h; HAUTEUR=1670 mm; HAUTEUR_COFFRET=1550 mm; HAUTEUR_SORTIE_AIR=1662 mm; LARGEUR=890 mm  [stored 2.91995 ft]; LARGEUR_COFFRET_GAUCHE=400 mm  [stored 1.31234 ft]; LARGEUR_SORTIE_AIR=10 mm  [stored 0.0328084 ft]; LONGUEUR=1870 mm; LONGUEUR_COFFRET_GAUCHE=1048 mm; MAINTENANCE_ZONE_ARRIERE=1593 mm; MAINTENANCE_ZONE_AVANT=792.5 mm; MAINTENANCE_ZONE_GAUCHE-DROITE=2400 mm; MAINTENANCE_ZONE_HAUTEUR=2250 mm; NEUTRE_COFFRET_CONNEXION_X'=Non; NEUTRE_COFFRET_CONNEXION_Y'=Non; NEUTRE_COFFRET_X=Non; NEUTRE_COFFRET_Y=Non; NIVEAU_SONORE(dB(A))=67; POIDS(Kg)=650 mm  [stored 2.13255 ft]; PUISS_APPARENTE_COFFRET=0 VA; PUISS_APPARENTE_COFFRET'=0 VA; PUISS_APPARENTE_COMPRESSEUR=20556 VA; PUISS_ELECT_COMPRESSEUR=19 kW; TENSION_ALIM_COFFRET=0 V; Zone de maintenance=Oui
- HOSPITAIR PACK - 15 bar - MVC23 - Secondaire: BRANCHEMENT_TERRE_COFFRET_CONNEXION_X'=Non; BRANCHEMENT_TERRE_COFFRET_CONNEXION_Y'=Non; BRANCHEMENT_TERRE_COFFRET_X=Non; BRANCHEMENT_TERRE_COFFRET_Y=Non; BRANCHEMENT_TERRE_COMPRESSEUR=Oui; COFFRET ELEC STANDARD PM2=Non; COMPRESSEUR=HOSPITAIR G - MVX 4-5 - MVA 9 - MVB 12-16 - MVC 19-23 : MVC 23; CONNEXION X'_Y'=Non; Chaine de traitement ...AD5035=Non; Chaine de traitement ...AD5065=Non; Chaine de traitement ...AD5130=Non; Chaine de traitement ...AD5195=Oui; DESCR_ALIM_COFFRET_CONNEXION_X'=NE PAS UTILISER; DESCR_ALIM_COFFRET_CONNEXION_Y'=NE PAS UTILISER; DESCR_ALIM_COFFRET_X=NE PAS UTILISER; DESCR_ALIM_COFFRET_Y=NE PAS UTILISER; DESCR_ALIM_COMPRESSEUR=Alimentation électrique, 4G16mm²; DESCR_REFOUL=Refoulement Air; 174m3/h; G3/4"FEM; DIAM_REFOUL_AIR=20 mm  [stored 0.0656168 ft]; Debit_refoulement_air=174.0 m³/h; HAUTEUR=1670 mm; HAUTEUR_COFFRET=1550 mm; HAUTEUR_SORTIE_AIR=1662 mm; LARGEUR=890 mm  [stored 2.91995 ft]; LARGEUR_COFFRET_GAUCHE=400 mm  [stored 1.31234 ft]; LARGEUR_SORTIE_AIR=10 mm  [stored 0.0328084 ft]; LONGUEUR=1870 mm; LONGUEUR_COFFRET_GAUCHE=1048 mm; MAINTENANCE_ZONE_ARRIERE=1593 mm; MAINTENANCE_ZONE_AVANT=792.5 mm; MAINTENANCE_ZONE_GAUCHE-DROITE=2400 mm; MAINTENANCE_ZONE_HAUTEUR=2250 mm; NEUTRE_COFFRET_CONNEXION_X'=Non; NEUTRE_COFFRET_CONNEXION_Y'=Non; NEUTRE_COFFRET_X=Non; NEUTRE_COFFRET_Y=Non; NIVEAU_SONORE(dB(A))=69; POIDS(Kg)=680 mm  [stored 2.23097 ft]; PUISS_APPARENTE_COFFRET=0 VA; PUISS_APPARENTE_COFFRET'=0 VA; PUISS_APPARENTE_COMPRESSEUR=24444 VA; PUISS_ELECT_COMPRESSEUR=22 kW; TENSION_ALIM_COFFRET=0 V; Zone de maintenance=Oui
- HOSPITAIR PACK - 15 bar - MVX4 - Principal: BRANCHEMENT_TERRE_COFFRET_CONNEXION_X'=Non; BRANCHEMENT_TERRE_COFFRET_CONNEXION_Y'=Non; BRANCHEMENT_TERRE_COFFRET_X=Oui; BRANCHEMENT_TERRE_COFFRET_Y=Oui; BRANCHEMENT_TERRE_COMPRESSEUR=Oui; COFFRET ELEC STANDARD PM2=Oui; COMPRESSEUR=HOSPITAIR G - MVX 4-5 - MVA 9 - MVB 12-16 - MVC 19-23 : MVX 4; CONNEXION X'_Y'=Non; Chaine de traitement ...AD5035=Oui; Chaine de traitement ...AD5065=Non; Chaine de traitement ...AD5130=Non; Chaine de traitement ...AD5195=Non; DESCR_ALIM_COFFRET_CONNEXION_X'=NE PAS UTILISER; DESCR_ALIM_COFFRET_CONNEXION_Y'=NE PAS UTILISER; DESCR_ALIM_COFFRET_X=Alimentation électrique, 3G0.75mm²; DESCR_ALIM_COFFRET_Y=Alimentation électrique, 3G0.75mm²; DESCR_ALIM_COMPRESSEUR=Alimentation électrique, 4G2.5mm²; DESCR_REFOUL=Refoulement Air; 22m3/h; G1/2"FEM; DIAM_REFOUL_AIR=15 mm  [stored 0.0492126 ft]; Debit_refoulement_air=22.0 m³/h; HAUTEUR=1340 mm; HAUTEUR_COFFRET=1080 mm  [stored 3.54331 ft]; HAUTEUR_SORTIE_AIR=1372 mm; LARGEUR=600 mm  [stored 1.9685 ft]; LARGEUR_COFFRET_GAUCHE=300 mm  [stored 0.984252 ft]; LARGEUR_SORTIE_AIR=25 mm  [stored 0.082021 ft]; LONGUEUR=860 mm; LONGUEUR_COFFRET_GAUCHE=344 mm; MAINTENANCE_ZONE_ARRIERE=1135 mm; MAINTENANCE_ZONE_AVANT=720 mm; MAINTENANCE_ZONE_GAUCHE-DROITE=2190 mm; MAINTENANCE_ZONE_HAUTEUR=1780 mm; NEUTRE_COFFRET_CONNEXION_X'=Non; NEUTRE_COFFRET_CONNEXION_Y'=Non; NEUTRE_COFFRET_X=Oui; NEUTRE_COFFRET_Y=Oui; NIVEAU_SONORE(dB(A))=62; POIDS(Kg)=170 mm  [stored 0.557743 ft]; PUISS_APPARENTE_COFFRET=333 VA; PUISS_APPARENTE_COFFRET'=0 VA; PUISS_APPARENTE_COMPRESSEUR=4444 VA; PUISS_ELECT_COMPRESSEUR=4 kW; TENSION_ALIM_COFFRET=230 V; Zone de maintenance=Oui
- HOSPITAIR PACK - 15 bar - MVX4 - Secondaire: BRANCHEMENT_TERRE_COFFRET_CONNEXION_X'=Non; BRANCHEMENT_TERRE_COFFRET_CONNEXION_Y'=Non; BRANCHEMENT_TERRE_COFFRET_X=Non; BRANCHEMENT_TERRE_COFFRET_Y=Non; BRANCHEMENT_TERRE_COMPRESSEUR=Oui; COFFRET ELEC STANDARD PM2=Non; COMPRESSEUR=HOSPITAIR G - MVX 4-5 - MVA 9 - MVB 12-16 - MVC 19-23 : MVX 4; CONNEXION X'_Y'=Non; Chaine de traitement ...AD5035=Oui; Chaine de traitement ...AD5065=Non; Chaine de traitement ...AD5130=Non; Chaine de traitement ...AD5195=Non; DESCR_ALIM_COFFRET_CONNEXION_X'=NE PAS UTILISER; DESCR_ALIM_COFFRET_CONNEXION_Y'=NE PAS UTILISER; DESCR_ALIM_COFFRET_X=NE PAS UTILISER; DESCR_ALIM_COFFRET_Y=NE PAS UTILISER; DESCR_ALIM_COMPRESSEUR=Alimentation électrique, 4G2.5mm²; DESCR_REFOUL=Refoulement Air; 22m3/h; G1/2"FEM; DIAM_REFOUL_AIR=15 mm  [stored 0.0492126 ft]; Debit_refoulement_air=22.0 m³/h; HAUTEUR=1340 mm; HAUTEUR_COFFRET=1080 mm  [stored 3.54331 ft]; HAUTEUR_SORTIE_AIR=1372 mm; LARGEUR=600 mm  [stored 1.9685 ft]; LARGEUR_COFFRET_GAUCHE=300 mm  [stored 0.984252 ft]; LARGEUR_SORTIE_AIR=25 mm  [stored 0.082021 ft]; LONGUEUR=860 mm; LONGUEUR_COFFRET_GAUCHE=344 mm; MAINTENANCE_ZONE_ARRIERE=1135 mm; MAINTENANCE_ZONE_AVANT=720 mm; MAINTENANCE_ZONE_GAUCHE-DROITE=2190 mm; MAINTENANCE_ZONE_HAUTEUR=1780 mm; NEUTRE_COFFRET_CONNEXION_X'=Non; NEUTRE_COFFRET_CONNEXION_Y'=Non; NEUTRE_COFFRET_X=Non; NEUTRE_COFFRET_Y=Non; NIVEAU_SONORE(dB(A))=62; POIDS(Kg)=160 mm  [stored 0.524934 ft]; PUISS_APPARENTE_COFFRET=0 VA; PUISS_APPARENTE_COFFRET'=0 VA; PUISS_APPARENTE_COMPRESSEUR=4444 VA; PUISS_ELECT_COMPRESSEUR=4 kW; TENSION_ALIM_COFFRET=0 V; Zone de maintenance=Oui
- HOSPITAIR PACK - 15 bar - MVX5 - Principal: BRANCHEMENT_TERRE_COFFRET_CONNEXION_X'=Non; BRANCHEMENT_TERRE_COFFRET_CONNEXION_Y'=Non; BRANCHEMENT_TERRE_COFFRET_X=Oui; BRANCHEMENT_TERRE_COFFRET_Y=Oui; BRANCHEMENT_TERRE_COMPRESSEUR=Oui; COFFRET ELEC STANDARD PM2=Oui; COMPRESSEUR=HOSPITAIR G - MVX 4-5 - MVA 9 - MVB 12-16 - MVC 19-23 : MVX 5; CONNEXION X'_Y'=Non; Chaine de traitement ...AD5035=Oui; Chaine de traitement ...AD5065=Non; Chaine de traitement ...AD5130=Non; Chaine de traitement ...AD5195=Non; DESCR_ALIM_COFFRET_CONNEXION_X'=NE PAS UTILISER; DESCR_ALIM_COFFRET_CONNEXION_Y'=NE PAS UTILISER; DESCR_ALIM_COFFRET_X=Alimentation électrique, 3G0.75mm²; DESCR_ALIM_COFFRET_Y=Alimentation électrique, 3G0.75mm²; DESCR_ALIM_COMPRESSEUR=Alimentation électrique, 4G2.5mm²; DESCR_REFOUL=Refoulement Air; 32m3/h; G1/2"FEM; DIAM_REFOUL_AIR=15 mm  [stored 0.0492126 ft]; Debit_refoulement_air=32.0 m³/h; HAUTEUR=1430 mm; HAUTEUR_COFFRET=1080 mm  [stored 3.54331 ft]; HAUTEUR_SORTIE_AIR=1372 mm; LARGEUR=600 mm  [stored 1.9685 ft]; LARGEUR_COFFRET_GAUCHE=300 mm  [stored 0.984252 ft]; LARGEUR_SORTIE_AIR=25 mm  [stored 0.082021 ft]; LONGUEUR=870 mm  [stored 2.85433 ft]; LONGUEUR_COFFRET_GAUCHE=344 mm; MAINTENANCE_ZONE_ARRIERE=1135 mm; MAINTENANCE_ZONE_AVANT=720 mm; MAINTENANCE_ZONE_GAUCHE-DROITE=2190 mm; MAINTENANCE_ZONE_HAUTEUR=2065 mm; NEUTRE_COFFRET_CONNEXION_X'=Non; NEUTRE_COFFRET_CONNEXION_Y'=Non; NEUTRE_COFFRET_X=Oui; NEUTRE_COFFRET_Y=Oui; NIVEAU_SONORE(dB(A))=64; POIDS(Kg)=185 mm  [stored 0.606955 ft]; PUISS_APPARENTE_COFFRET=333 VA; PUISS_APPARENTE_COFFRET'=0 VA; PUISS_APPARENTE_COMPRESSEUR=6111 VA; PUISS_ELECT_COMPRESSEUR=6 kW; TENSION_ALIM_COFFRET=230 V; Zone de maintenance=Oui
- HOSPITAIR PACK - 15 bar - MVX5 - Secondaire: BRANCHEMENT_TERRE_COFFRET_CONNEXION_X'=Non; BRANCHEMENT_TERRE_COFFRET_CONNEXION_Y'=Non; BRANCHEMENT_TERRE_COFFRET_X=Non; BRANCHEMENT_TERRE_COFFRET_Y=Non; BRANCHEMENT_TERRE_COMPRESSEUR=Oui; COFFRET ELEC STANDARD PM2=Non; COMPRESSEUR=HOSPITAIR G - MVX 4-5 - MVA 9 - MVB 12-16 - MVC 19-23 : MVX 5; CONNEXION X'_Y'=Non; Chaine de traitement ...AD5035=Oui; Chaine de traitement ...AD5065=Non; Chaine de traitement ...AD5130=Non; Chaine de traitement ...AD5195=Non; DESCR_ALIM_COFFRET_CONNEXION_X'=NE PAS UTILISER; DESCR_ALIM_COFFRET_CONNEXION_Y'=NE PAS UTILISER; DESCR_ALIM_COFFRET_X=NE PAS UTILISER; DESCR_ALIM_COFFRET_Y=NE PAS UTILISER; DESCR_ALIM_COMPRESSEUR=Alimentation électrique, 4G2.5mm²; DESCR_REFOUL=Refoulement Air; 32m3/h; G1/2"FEM; DIAM_REFOUL_AIR=15 mm  [stored 0.0492126 ft]; Debit_refoulement_air=32.0 m³/h; HAUTEUR=1430 mm; HAUTEUR_COFFRET=1080 mm  [stored 3.54331 ft]; HAUTEUR_SORTIE_AIR=1372 mm; LARGEUR=600 mm  [stored 1.9685 ft]; LARGEUR_COFFRET_GAUCHE=300 mm  [stored 0.984252 ft]; LARGEUR_SORTIE_AIR=25 mm  [stored 0.082021 ft]; LONGUEUR=870 mm  [stored 2.85433 ft]; LONGUEUR_COFFRET_GAUCHE=344 mm; MAINTENANCE_ZONE_ARRIERE=1135 mm; MAINTENANCE_ZONE_AVANT=720 mm; MAINTENANCE_ZONE_GAUCHE-DROITE=2190 mm; MAINTENANCE_ZONE_HAUTEUR=2065 mm; NEUTRE_COFFRET_CONNEXION_X'=Non; NEUTRE_COFFRET_CONNEXION_Y'=Non; NEUTRE_COFFRET_X=Non; NEUTRE_COFFRET_Y=Non; NIVEAU_SONORE(dB(A))=64; POIDS(Kg)=175 mm  [stored 0.574147 ft]; PUISS_APPARENTE_COFFRET=0 VA; PUISS_APPARENTE_COFFRET'=0 VA; PUISS_APPARENTE_COMPRESSEUR=6111 VA; PUISS_ELECT_COMPRESSEUR=6 kW; TENSION_ALIM_COFFRET=0 V; Zone de maintenance=Oui
- HOSPITAIR PACK - 15 bar - MVA9 - Principal: BRANCHEMENT_TERRE_COFFRET_CONNEXION_X'=Non; BRANCHEMENT_TERRE_COFFRET_CONNEXION_Y'=Non; BRANCHEMENT_TERRE_COFFRET_X=Oui; BRANCHEMENT_TERRE_COFFRET_Y=Oui; BRANCHEMENT_TERRE_COMPRESSEUR=Oui; COFFRET ELEC STANDARD PM2=Oui; COMPRESSEUR=HOSPITAIR G - MVX 4-5 - MVA 9 - MVB 12-16 - MVC 19-23 : MVA 9; CONNEXION X'_Y'=Non; Chaine de traitement ...AD5035=Non; Chaine de traitement ...AD5065=Oui; Chaine de traitement ...AD5130=Non; Chaine de traitement ...AD5195=Non; DESCR_ALIM_COFFRET_CONNEXION_X'=NE PAS UTILISER; DESCR_ALIM_COFFRET_CONNEXION_Y'=NE PAS UTILISER; DESCR_ALIM_COFFRET_X=Alimentation électrique, 3G0.75mm²; DESCR_ALIM_COFFRET_Y=Alimentation électrique, 3G0.75mm²; DESCR_ALIM_COMPRESSEUR=Alimentation électrique, 4G4mm²; DESCR_REFOUL=Refoulement Air; 50m3/h; G1/2"FEM; DIAM_REFOUL_AIR=15 mm  [stored 0.0492126 ft]; Debit_refoulement_air=50.0 m³/h; HAUTEUR=1630 mm; HAUTEUR_COFFRET=1365 mm; HAUTEUR_SORTIE_AIR=1662 mm; LARGEUR=640 mm  [stored 2.09974 ft]; LARGEUR_COFFRET_GAUCHE=300 mm  [stored 0.984252 ft]; LARGEUR_SORTIE_AIR=20 mm  [stored 0.0656168 ft]; LONGUEUR=1000 mm  [stored 3.28084 ft]; LONGUEUR_COFFRET_GAUCHE=344 mm; MAINTENANCE_ZONE_ARRIERE=1293 mm; MAINTENANCE_ZONE_AVANT=720 mm; MAINTENANCE_ZONE_GAUCHE-DROITE=2230 mm; MAINTENANCE_ZONE_HAUTEUR=2065 mm; NEUTRE_COFFRET_CONNEXION_X'=Non; NEUTRE_COFFRET_CONNEXION_Y'=Non; NEUTRE_COFFRET_X=Oui; NEUTRE_COFFRET_Y=Oui; NIVEAU_SONORE(dB(A))=65; POIDS(Kg)=290 mm  [stored 0.951444 ft]; PUISS_APPARENTE_COFFRET=333 VA; PUISS_APPARENTE_COFFRET'=0 VA; PUISS_APPARENTE_COMPRESSEUR=8333 VA; PUISS_ELECT_COMPRESSEUR=8 kW; TENSION_ALIM_COFFRET=230 V; Zone de maintenance=Oui
- HOSPITAIR PACK - 15 bar - MVA9 - Secondaire: BRANCHEMENT_TERRE_COFFRET_CONNEXION_X'=Non; BRANCHEMENT_TERRE_COFFRET_CONNEXION_Y'=Non; BRANCHEMENT_TERRE_COFFRET_X=Non; BRANCHEMENT_TERRE_COFFRET_Y=Non; BRANCHEMENT_TERRE_COMPRESSEUR=Oui; COFFRET ELEC STANDARD PM2=Non; COMPRESSEUR=HOSPITAIR G - MVX 4-5 - MVA 9 - MVB 12-16 - MVC 19-23 : MVA 9; CONNEXION X'_Y'=Non; Chaine de traitement ...AD5035=Non; Chaine de traitement ...AD5065=Oui; Chaine de traitement ...AD5130=Non; Chaine de traitement ...AD5195=Non; DESCR_ALIM_COFFRET_CONNEXION_X'=NE PAS UTILISER; DESCR_ALIM_COFFRET_CONNEXION_Y'=NE PAS UTILISER; DESCR_ALIM_COFFRET_X=NE PAS UTILISER; DESCR_ALIM_COFFRET_Y=NE PAS UTILISER; DESCR_ALIM_COMPRESSEUR=Alimentation électrique, 4G4mm²; DESCR_REFOUL=Refoulement Air; 50m3/h; G1/2"FEM; DIAM_REFOUL_AIR=15 mm  [stored 0.0492126 ft]; Debit_refoulement_air=50.0 m³/h; HAUTEUR=1630 mm; HAUTEUR_COFFRET=1365 mm; HAUTEUR_SORTIE_AIR=1662 mm; LARGEUR=640 mm  [stored 2.09974 ft]; LARGEUR_COFFRET_GAUCHE=300 mm  [stored 0.984252 ft]; LARGEUR_SORTIE_AIR=20 mm  [stored 0.0656168 ft]; LONGUEUR=1000 mm  [stored 3.28084 ft]; LONGUEUR_COFFRET_GAUCHE=344 mm; MAINTENANCE_ZONE_ARRIERE=1293 mm; MAINTENANCE_ZONE_AVANT=720 mm; MAINTENANCE_ZONE_GAUCHE-DROITE=2230 mm; MAINTENANCE_ZONE_HAUTEUR=2065 mm; NEUTRE_COFFRET_CONNEXION_X'=Non; NEUTRE_COFFRET_CONNEXION_Y'=Non; NEUTRE_COFFRET_X=Non; NEUTRE_COFFRET_Y=Non; NIVEAU_SONORE(dB(A))=65; POIDS(Kg)=280 mm  [stored 0.918635 ft]; PUISS_APPARENTE_COFFRET=0 VA; PUISS_APPARENTE_COFFRET'=0 VA; PUISS_APPARENTE_COMPRESSEUR=8333 VA; PUISS_ELECT_COMPRESSEUR=8 kW; TENSION_ALIM_COFFRET=0 V; Zone de maintenance=Oui
- HOSPITAIR PACK - 15 bar - MVB12 - Principal: BRANCHEMENT_TERRE_COFFRET_CONNEXION_X'=Non; BRANCHEMENT_TERRE_COFFRET_CONNEXION_Y'=Non; BRANCHEMENT_TERRE_COFFRET_X=Oui; BRANCHEMENT_TERRE_COFFRET_Y=Oui; BRANCHEMENT_TERRE_COMPRESSEUR=Oui; COFFRET ELEC STANDARD PM2=Oui; COMPRESSEUR=HOSPITAIR G - MVX 4-5 - MVA 9 - MVB 12-16 - MVC 19-23 : MVB 12; CONNEXION X'_Y'=Non; Chaine de traitement ...AD5035=Non; Chaine de traitement ...AD5065=Oui; Chaine de traitement ...AD5130=Non; Chaine de traitement ...AD5195=Non; DESCR_ALIM_COFFRET_CONNEXION_X'=NE PAS UTILISER; DESCR_ALIM_COFFRET_CONNEXION_Y'=NE PAS UTILISER; DESCR_ALIM_COFFRET_X=Alimentation électrique, 3G0.75mm²; DESCR_ALIM_COFFRET_Y=Alimentation électrique, 3G0.75mm²; DESCR_ALIM_COMPRESSEUR=Alimentation électrique, 4G6mm²; DESCR_REFOUL=Refoulement Air; 78m3/h; G3/4"FEM; DIAM_REFOUL_AIR=20 mm  [stored 0.0656168 ft]; Debit_refoulement_air=78.0 m³/h; HAUTEUR=1350 mm; HAUTEUR_COFFRET=1365 mm; HAUTEUR_SORTIE_AIR=1662 mm; LARGEUR=750 mm  [stored 2.46063 ft]; LARGEUR_COFFRET_GAUCHE=370 mm  [stored 1.21391 ft]; LARGEUR_SORTIE_AIR=20 mm  [stored 0.0656168 ft]; LONGUEUR=1100 mm; LONGUEUR_COFFRET_GAUCHE=344 mm; MAINTENANCE_ZONE_ARRIERE=1398 mm; MAINTENANCE_ZONE_AVANT=792.5 mm; MAINTENANCE_ZONE_GAUCHE-DROITE=2350 mm; MAINTENANCE_ZONE_HAUTEUR=2065 mm; NEUTRE_COFFRET_CONNEXION_X'=Non; NEUTRE_COFFRET_CONNEXION_Y'=Non; NEUTRE_COFFRET_X=Oui; NEUTRE_COFFRET_Y=Oui; NIVEAU_SONORE(dB(A))=64; POIDS(Kg)=375 mm  [stored 1.23031 ft]; PUISS_APPARENTE_COFFRET=333 VA; PUISS_APPARENTE_COFFRET'=0 VA; PUISS_APPARENTE_COMPRESSEUR=12222 VA; PUISS_ELECT_COMPRESSEUR=11 kW; TENSION_ALIM_COFFRET=230 V; Zone de maintenance=Oui
- HOSPITAIR PACK - 15 bar - MVB12 - Secondaire: BRANCHEMENT_TERRE_COFFRET_CONNEXION_X'=Non; BRANCHEMENT_TERRE_COFFRET_CONNEXION_Y'=Non; BRANCHEMENT_TERRE_COFFRET_X=Non; BRANCHEMENT_TERRE_COFFRET_Y=Non; BRANCHEMENT_TERRE_COMPRESSEUR=Oui; COFFRET ELEC STANDARD PM2=Non; COMPRESSEUR=HOSPITAIR G - MVX 4-5 - MVA 9 - MVB 12-16 - MVC 19-23 : MVB 12; CONNEXION X'_Y'=Non; Chaine de traitement ...AD5035=Non; Chaine de traitement ...AD5065=Oui; Chaine de traitement ...AD5130=Non; Chaine de traitement ...AD5195=Non; DESCR_ALIM_COFFRET_CONNEXION_X'=NE PAS UTILISER; DESCR_ALIM_COFFRET_CONNEXION_Y'=NE PAS UTILISER; DESCR_ALIM_COFFRET_X=NE PAS UTILISER; DESCR_ALIM_COFFRET_Y=NE PAS UTILISER; DESCR_ALIM_COMPRESSEUR=Alimentation électrique, 4G6mm²; DESCR_REFOUL=Refoulement Air; 78m3/h; G3/4"FEM; DIAM_REFOUL_AIR=20 mm  [stored 0.0656168 ft]; Debit_refoulement_air=78.0 m³/h; HAUTEUR=1350 mm; HAUTEUR_COFFRET=1365 mm; HAUTEUR_SORTIE_AIR=1662 mm; LARGEUR=750 mm  [stored 2.46063 ft]; LARGEUR_COFFRET_GAUCHE=370 mm  [stored 1.21391 ft]; LARGEUR_SORTIE_AIR=20 mm  [stored 0.0656168 ft]; LONGUEUR=1100 mm; LONGUEUR_COFFRET_GAUCHE=344 mm; MAINTENANCE_ZONE_ARRIERE=1398 mm; MAINTENANCE_ZONE_AVANT=792.5 mm; MAINTENANCE_ZONE_GAUCHE-DROITE=2350 mm; MAINTENANCE_ZONE_HAUTEUR=2065 mm; NEUTRE_COFFRET_CONNEXION_X'=Non; NEUTRE_COFFRET_CONNEXION_Y'=Non; NEUTRE_COFFRET_X=Non; NEUTRE_COFFRET_Y=Non; NIVEAU_SONORE(dB(A))=64; POIDS(Kg)=365 mm  [stored 1.19751 ft]; PUISS_APPARENTE_COFFRET=0 VA; PUISS_APPARENTE_COFFRET'=0 VA; PUISS_APPARENTE_COMPRESSEUR=12222 VA; PUISS_ELECT_COMPRESSEUR=11 kW; TENSION_ALIM_COFFRET=0 V; Zone de maintenance=Oui
- HOSPITAIR PACK - 15 bar - MVB16 - Principal: BRANCHEMENT_TERRE_COFFRET_CONNEXION_X'=Non; BRANCHEMENT_TERRE_COFFRET_CONNEXION_Y'=Non; BRANCHEMENT_TERRE_COFFRET_X=Oui; BRANCHEMENT_TERRE_COFFRET_Y=Oui; BRANCHEMENT_TERRE_COMPRESSEUR=Oui; COFFRET ELEC STANDARD PM2=Oui; COMPRESSEUR=HOSPITAIR G - MVX 4-5 - MVA 9 - MVB 12-16 - MVC 19-23 : MVB 16; CONNEXION X'_Y'=Non; Chaine de traitement ...AD5035=Non; Chaine de traitement ...AD5065=Non; Chaine de traitement ...AD5130=Oui; Chaine de traitement ...AD5195=Non; DESCR_ALIM_COFFRET_CONNEXION_X'=NE PAS UTILISER; DESCR_ALIM_COFFRET_CONNEXION_Y'=NE PAS UTILISER; DESCR_ALIM_COFFRET_X=Alimentation électrique, 3G0.75mm²; DESCR_ALIM_COFFRET_Y=Alimentation électrique, 3G0.75mm²; DESCR_ALIM_COMPRESSEUR=Alimentation électrique, 4G10mm²; DESCR_REFOUL=Refoulement Air; 102m3/h; G3/4"FEM; DIAM_REFOUL_AIR=20 mm  [stored 0.0656168 ft]; Debit_refoulement_air=102.0 m³/h; HAUTEUR=1350 mm; HAUTEUR_COFFRET=1365 mm; HAUTEUR_SORTIE_AIR=1662 mm; LARGEUR=750 mm  [stored 2.46063 ft]; LARGEUR_COFFRET_GAUCHE=370 mm  [stored 1.21391 ft]; LARGEUR_SORTIE_AIR=95 mm  [stored 0.31168 ft]; LONGUEUR=1250 mm  [stored 4.10105 ft]; LONGUEUR_COFFRET_GAUCHE=344 mm; MAINTENANCE_ZONE_ARRIERE=1398 mm; MAINTENANCE_ZONE_AVANT=792.5 mm; MAINTENANCE_ZONE_GAUCHE-DROITE=2350 mm; MAINTENANCE_ZONE_HAUTEUR=2065 mm; NEUTRE_COFFRET_CONNEXION_X'=Non; NEUTRE_COFFRET_CONNEXION_Y'=Non; NEUTRE_COFFRET_X=Oui; NEUTRE_COFFRET_Y=Oui; NIVEAU_SONORE(dB(A))=65; POIDS(Kg)=480 mm  [stored 1.5748 ft]; PUISS_APPARENTE_COFFRET=333 VA; PUISS_APPARENTE_COFFRET'=0 VA; PUISS_APPARENTE_COMPRESSEUR=16667 VA; PUISS_ELECT_COMPRESSEUR=15 kW; TENSION_ALIM_COFFRET=230 V; Zone de maintenance=Oui
- HOSPITAIR PACK - 15 bar - MVB16 - Secondaire: BRANCHEMENT_TERRE_COFFRET_CONNEXION_X'=Non; BRANCHEMENT_TERRE_COFFRET_CONNEXION_Y'=Non; BRANCHEMENT_TERRE_COFFRET_X=Non; BRANCHEMENT_TERRE_COFFRET_Y=Non; BRANCHEMENT_TERRE_COMPRESSEUR=Oui; COFFRET ELEC STANDARD PM2=Non; COMPRESSEUR=HOSPITAIR G - MVX 4-5 - MVA 9 - MVB 12-16 - MVC 19-23 : MVB 16; CONNEXION X'_Y'=Non; Chaine de traitement ...AD5035=Non; Chaine de traitement ...AD5065=Non; Chaine de traitement ...AD5130=Oui; Chaine de traitement ...AD5195=Non; DESCR_ALIM_COFFRET_CONNEXION_X'=NE PAS UTILISER; DESCR_ALIM_COFFRET_CONNEXION_Y'=NE PAS UTILISER; DESCR_ALIM_COFFRET_X=NE PAS UTILISER; DESCR_ALIM_COFFRET_Y=NE PAS UTILISER; DESCR_ALIM_COMPRESSEUR=Alimentation électrique, 4G10mm²; DESCR_REFOUL=Refoulement Air; 102m3/h; G3/4"FEM; DIAM_REFOUL_AIR=20 mm  [stored 0.0656168 ft]; Debit_refoulement_air=102.0 m³/h; HAUTEUR=1350 mm; HAUTEUR_COFFRET=1365 mm; HAUTEUR_SORTIE_AIR=1662 mm; LARGEUR=750 mm  [stored 2.46063 ft]; LARGEUR_COFFRET_GAUCHE=370 mm  [stored 1.21391 ft]; LARGEUR_SORTIE_AIR=95 mm  [stored 0.31168 ft]; LONGUEUR=1250 mm  [stored 4.10105 ft]; LONGUEUR_COFFRET_GAUCHE=344 mm; MAINTENANCE_ZONE_ARRIERE=1398 mm; MAINTENANCE_ZONE_AVANT=792.5 mm; MAINTENANCE_ZONE_GAUCHE-DROITE=2350 mm; MAINTENANCE_ZONE_HAUTEUR=2065 mm; NEUTRE_COFFRET_CONNEXION_X'=Non; NEUTRE_COFFRET_CONNEXION_Y'=Non; NEUTRE_COFFRET_X=Non; NEUTRE_COFFRET_Y=Non; NIVEAU_SONORE(dB(A))=65; POIDS(Kg)=470 mm  [stored 1.54199 ft]; PUISS_APPARENTE_COFFRET=0 VA; PUISS_APPARENTE_COFFRET'=0 VA; PUISS_APPARENTE_COMPRESSEUR=16667 VA; PUISS_ELECT_COMPRESSEUR=15 kW; TENSION_ALIM_COFFRET=0 V; Zone de maintenance=Oui
- HOSPITAIR PACK - 15 bar - MVC19 - Principal: BRANCHEMENT_TERRE_COFFRET_CONNEXION_X'=Oui; BRANCHEMENT_TERRE_COFFRET_CONNEXION_Y'=Oui; BRANCHEMENT_TERRE_COFFRET_X=Non; BRANCHEMENT_TERRE_COFFRET_Y=Non; BRANCHEMENT_TERRE_COMPRESSEUR=Oui; COFFRET ELEC STANDARD PM2=Oui; COMPRESSEUR=HOSPITAIR G - MVX 4-5 - MVA 9 - MVB 12-16 - MVC 19-23 : MVC 19; CONNEXION X'_Y'=Oui; Chaine de traitement ...AD5035=Non; Chaine de traitement ...AD5065=Non; Chaine de traitement ...AD5130=Oui; Chaine de traitement ...AD5195=Non; DESCR_ALIM_COFFRET_CONNEXION_X'=Alimentation électrique, 3G0.75mm²; DESCR_ALIM_COFFRET_CONNEXION_Y'=Alimentation électrique, 3G0.75mm²; DESCR_ALIM_COFFRET_X=NE PAS UTILISER; DESCR_ALIM_COFFRET_Y=NE PAS UTILISER; DESCR_ALIM_COMPRESSEUR=Alimentation électrique, 4G10mm²; DESCR_REFOUL=Refoulement Air; 150m3/h; G3/4"FEM; DIAM_REFOUL_AIR=20 mm  [stored 0.0656168 ft]; Debit_refoulement_air=150.0 m³/h; HAUTEUR=1670 mm; HAUTEUR_COFFRET=1550 mm; HAUTEUR_SORTIE_AIR=1662 mm; LARGEUR=890 mm  [stored 2.91995 ft]; LARGEUR_COFFRET_GAUCHE=300 mm  [stored 0.984252 ft]; LARGEUR_SORTIE_AIR=95 mm  [stored 0.31168 ft]; LONGUEUR=1870 mm; LONGUEUR_COFFRET_GAUCHE=1048 mm; MAINTENANCE_ZONE_ARRIERE=1593 mm; MAINTENANCE_ZONE_AVANT=792.5 mm; MAINTENANCE_ZONE_GAUCHE-DROITE=2400 mm; MAINTENANCE_ZONE_HAUTEUR=2250 mm; NEUTRE_COFFRET_CONNEXION_X'=Oui; NEUTRE_COFFRET_CONNEXION_Y'=Oui; NEUTRE_COFFRET_X=Non; NEUTRE_COFFRET_Y=Non; NIVEAU_SONORE(dB(A))=67; POIDS(Kg)=650 mm  [stored 2.13255 ft]; PUISS_APPARENTE_COFFRET=0 VA; PUISS_APPARENTE_COFFRET'=333 VA; PUISS_APPARENTE_COMPRESSEUR=20556 VA; PUISS_ELECT_COMPRESSEUR=19 kW; TENSION_ALIM_COFFRET=230 V; Zone de maintenance=Oui
- HOSPITAIR PACK - 15 bar - MVC19 - Secondaire: BRANCHEMENT_TERRE_COFFRET_CONNEXION_X'=Non; BRANCHEMENT_TERRE_COFFRET_CONNEXION_Y'=Non; BRANCHEMENT_TERRE_COFFRET_X=Non; BRANCHEMENT_TERRE_COFFRET_Y=Non; BRANCHEMENT_TERRE_COMPRESSEUR=Oui; COFFRET ELEC STANDARD PM2=Non; COMPRESSEUR=HOSPITAIR G - MVX 4-5 - MVA 9 - MVB 12-16 - MVC 19-23 : MVC 19; CONNEXION X'_Y'=Non; Chaine de traitement ...AD5035=Non; Chaine de traitement ...AD5065=Non; Chaine de traitement ...AD5130=Oui; Chaine de traitement ...AD5195=Non; DESCR_ALIM_COFFRET_CONNEXION_X'=NE PAS UTILISER; DESCR_ALIM_COFFRET_CONNEXION_Y'=NE PAS UTILISER; DESCR_ALIM_COFFRET_X=NE PAS UTILISER; DESCR_ALIM_COFFRET_Y=NE PAS UTILISER; DESCR_ALIM_COMPRESSEUR=Alimentation électrique, 4G10mm²; DESCR_REFOUL=Refoulement Air; 150m3/h; G3/4"FEM; DIAM_REFOUL_AIR=20 mm  [stored 0.0656168 ft]; Debit_refoulement_air=150.0 m³/h; HAUTEUR=1670 mm; HAUTEUR_COFFRET=1550 mm; HAUTEUR_SORTIE_AIR=1662 mm; LARGEUR=890 mm  [stored 2.91995 ft]; LARGEUR_COFFRET_GAUCHE=300 mm  [stored 0.984252 ft]; LARGEUR_SORTIE_AIR=95 mm  [stored 0.31168 ft]; LONGUEUR=1870 mm; LONGUEUR_COFFRET_GAUCHE=1048 mm; MAINTENANCE_ZONE_ARRIERE=1593 mm; MAINTENANCE_ZONE_AVANT=792.5 mm; MAINTENANCE_ZONE_GAUCHE-DROITE=2400 mm; MAINTENANCE_ZONE_HAUTEUR=2250 mm; NEUTRE_COFFRET_CONNEXION_X'=Non; NEUTRE_COFFRET_CONNEXION_Y'=Non; NEUTRE_COFFRET_X=Non; NEUTRE_COFFRET_Y=Non; NIVEAU_SONORE(dB(A))=67; POIDS(Kg)=650 mm  [stored 2.13255 ft]; PUISS_APPARENTE_COFFRET=0 VA; PUISS_APPARENTE_COFFRET'=0 VA; PUISS_APPARENTE_COMPRESSEUR=20556 VA; PUISS_ELECT_COMPRESSEUR=19 kW; TENSION_ALIM_COFFRET=0 V; Zone de maintenance=Oui

note: [stored X ft] marks values corroborated as IEEE doubles in the binary element streams (Revit-internal decimal feet)
